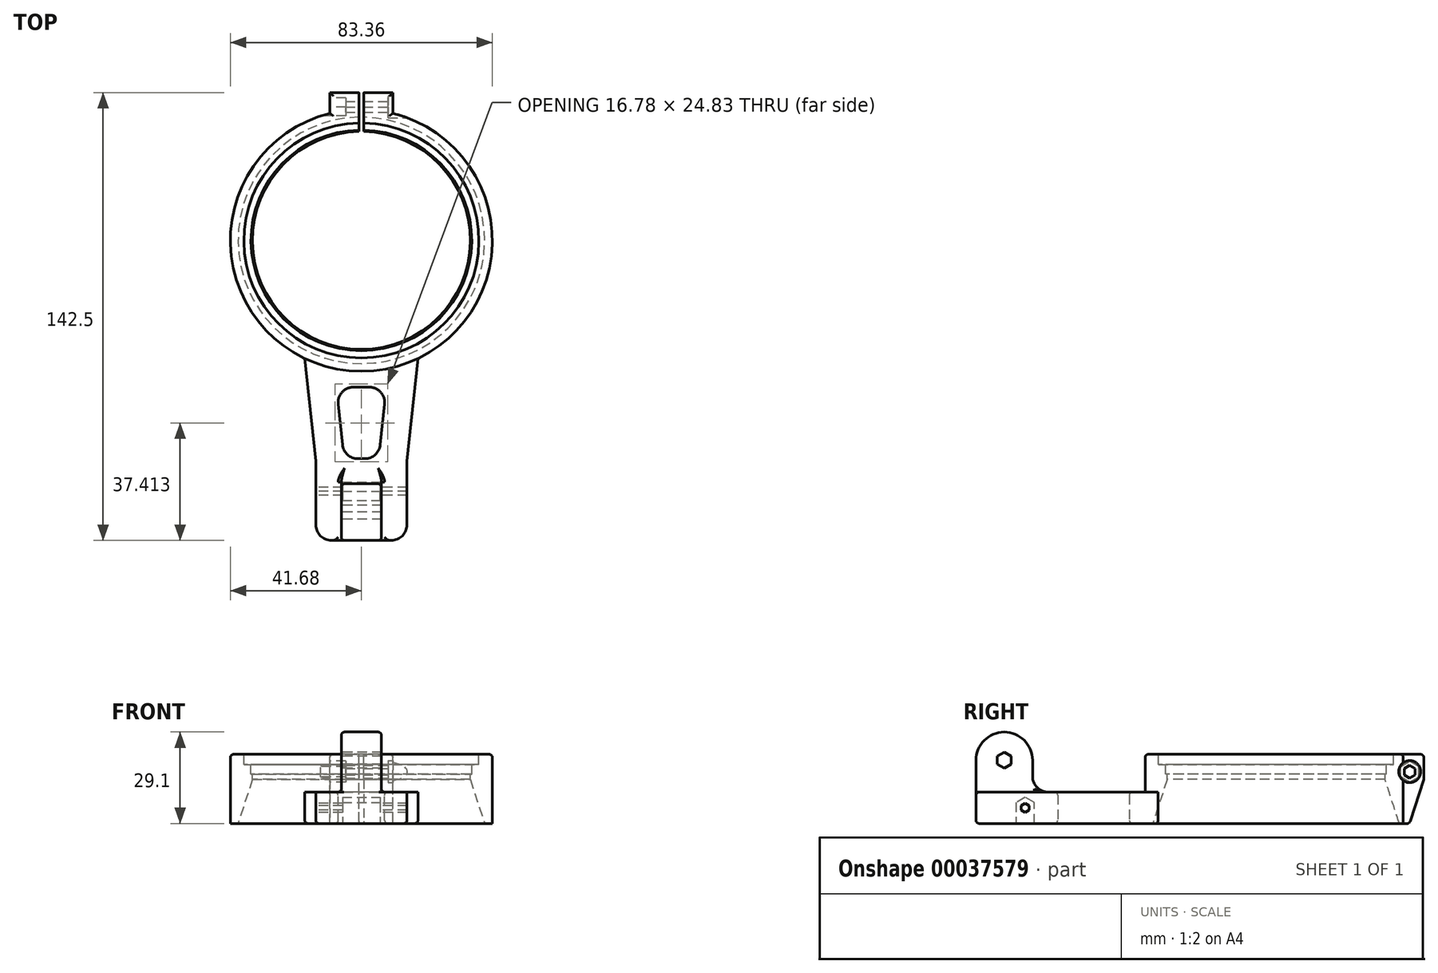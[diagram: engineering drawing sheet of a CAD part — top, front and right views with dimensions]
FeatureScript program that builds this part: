
annotation { "Feature Type Name" : "Feature", "Feature Type Description" : "" }
export const myFeature = defineFeature(function(context is Context, id is Id, definition is map)
    precondition{}
    {
        {
            var Q0;
            Q0=qCreatedBy(makeId("Right.planeOp"),FACE);
            var sketch = newSketch(context, id + "F0", { "sketchPlane" : qUnion([Q0])});
            skLineSegment(sketch, "E0", {"start": v(37.4, 0) * mm, "end": v(41.68, 0) * mm});
            skLineSegment(sketch, "E1", {"start": v(41.68, 0) * mm, "end": v(41.68, 22) * mm});
            skLineSegment(sketch, "E2", {"start": v(41.68, 22) * mm, "end": v(34.68, 22) * mm});
            skLineSegment(sketch, "E3", {"start": v(37.4, 3.3) * mm, "end": v(35.12, 3.3) * mm});
            skLineSegment(sketch, "E4", {"start": v(37.4, 3.3) * mm, "end": v(37.4, 0) * mm});
            skLineSegment(sketch, "E5", {"start": v(0, 0) * mm, "end": v(0, 55.42) * mm, "construction": true});
            skLineSegment(sketch, "E6", {"start": v(35.12, 3.3) * mm, "end": v(35.12, 6.3) * mm});
            skLineSegment(sketch, "E7", {"start": v(35.12, 6.3) * mm, "end": v(34.68, 6.3) * mm});
            skLineSegment(sketch, "E8", {"start": v(34.68, 6.3) * mm, "end": v(34.68, 22) * mm});
            skSolve(sketch);
        }
        {
            var Q0;
            Q0=makeQuery(id+"F0.imprint","IMPRINT",FACE,{"disambiguationData":[TD([[makeQuery(id+"F0.imprint","IMPRINT",EDGE,{"derivedFrom":sQuery(id+"F0.wireOp",EDGE,"E0")}),1.0]])]});
            var Q1;
            Q1=sQuery(id+"F0.wireOp",EDGE,"E5");
            revolve(context, id + "F1", {"entities" : qUnion([Q0]), "axis" : qUnion([Q1]), "revolveType" : RevolveType.FULL});
        }
        {
            var Q0;
            Q0=qCreatedBy(makeId("Top.planeOp"),FACE);
            var sketch = newSketch(context, id + "F2", { "sketchPlane" : qUnion([Q0])});
            skLineSegment(sketch, "E9.bottom", {"start": v(-0.75, 0) * mm, "end": v(0.75, 0) * mm});
            skLineSegment(sketch, "E9.top", {"start": v(-0.75, 47) * mm, "end": v(0.75, 47) * mm});
            skLineSegment(sketch, "E9.left", {"start": v(-0.75, 0) * mm, "end": v(-0.75, 47) * mm});
            skLineSegment(sketch, "E9.right", {"start": v(0.75, 0) * mm, "end": v(0.75, 47) * mm});
            skLineSegment(sketch, "E10", {"start": v(0, 0) * mm, "end": v(0, 47) * mm, "construction": true});
            skLineSegment(sketch, "E11.bottom", {"start": v(-10, 47) * mm, "end": v(10, 47) * mm});
            skLineSegment(sketch, "E11.top", {"start": v(-10, 40.46) * mm, "end": v(10, 40.46) * mm});
            skLineSegment(sketch, "E11.left", {"start": v(-10, 47) * mm, "end": v(-10, 40.46) * mm});
            skLineSegment(sketch, "E11.right", {"start": v(10, 47) * mm, "end": v(10, 40.46) * mm});
            skSolve(sketch);
        }
        {
            var Q0;
            {var subQ1=sQuery(id+"F2.wireOp",EDGE,"E11.left");Q0=makeQuery(id+"F2.imprint","IMPRINT",FACE,{"disambiguationData":[TD([[makeQuery(id+"F2.imprint","IMPRINT",EDGE,{"derivedFrom":subQ1}),1.0]])]});}
            var Q1;
            {var subQ3=sQuery(id+"F2.wireOp",EDGE,"E11.right");Q1=makeQuery(id+"F2.imprint","IMPRINT",FACE,{"disambiguationData":[TD([[makeQuery(id+"F2.imprint","IMPRINT",EDGE,{"derivedFrom":subQ3}),-1.0]])]});}
            var Q2;
            Q2=makeQuery(id+"F1.opRevolve","SWEPT_FACE",FACE,{"disambiguationData":[OSD([sQuery(id+"F0.wireOp",EDGE,"E2")])]});
            extrude(context, id + "F3", {"entities" : qUnion([Q0, Q1]), "operationType" : NewBodyOperationType.ADD, "endBound" : BoundingType.UP_TO_SURFACE, "endBoundEntityFace" : qUnion([Q2]), "depth" : 25 * mm});
        }
        {
            var Q0;
            {var subQ5=sQuery(id+"F2.wireOp",EDGE,"E9.bottom");Q0=makeQuery(id+"F2.imprint","IMPRINT",FACE,{"disambiguationData":[TD([[makeQuery(id+"F2.imprint","IMPRINT",EDGE,{"derivedFrom":subQ5}),1.0]])]});}
            var Q1;
            {var subQ0=sQuery(id+"F2.wireOp",EDGE,"E11.bottom");var subQ3=sQuery(id+"F2.wireOp",EDGE,"E9.left");var subQ4=makeQuery(id+"F2.imprint","INTERSECT",VERTEX,{"derivedFrom":[subQ3,subQ0]});Q1=makeQuery(id+"F2.imprint","IMPRINT",FACE,{"disambiguationData":[TD([[makeQuery(id+"F2.imprint","IMPRINT",EDGE,{"disambiguationData":[TD([[subQ4,1.0]])],"derivedFrom":subQ3}),-1.0]])]});}
            extrude(context, id + "F4", {"entities" : qUnion([Q0, Q1]), "operationType" : NewBodyOperationType.REMOVE, "endBound" : BoundingType.THROUGH_ALL, "depth" : 25 * mm});
        }
        {
            var Q0;
            Q0=makeQuery(id+"F3.opExtrude","SWEPT_FACE",FACE,{"disambiguationData":[OSD([sQuery(id+"F2.wireOp",EDGE,"E11.right")])]});
            var sketch = newSketch(context, id + "F5", { "sketchPlane" : qUnion([Q0])});
            skCircle(sketch, "E12", {"center": v(42.5, 5.5) * mm, "radius": 3.5 * mm});
            skCircle(sketch, "E13.cCircle", {"center": v(42.5, 5.5) * mm, "radius": 1.75 * mm, "construction": true});
            skLineSegment(sketch, "E13.0", {"start": v(44.25, 4.49) * mm, "end": v(42.5, 3.48) * mm});
            skLineSegment(sketch, "E13.1", {"start": v(42.5, 3.48) * mm, "end": v(40.75, 4.49) * mm});
            skLineSegment(sketch, "E13.2", {"start": v(40.75, 4.49) * mm, "end": v(40.75, 6.51) * mm});
            skLineSegment(sketch, "E13.3", {"start": v(40.75, 6.51) * mm, "end": v(42.5, 7.52) * mm});
            skLineSegment(sketch, "E13.4", {"start": v(42.5, 7.52) * mm, "end": v(44.25, 6.51) * mm});
            skLineSegment(sketch, "E13.5", {"start": v(44.25, 6.51) * mm, "end": v(44.25, 4.49) * mm});
            skPoint(sketch, "E13.0.midPoint", {"position": v(43.38, 3.98) * mm});
            skSolve(sketch);
        }
        {
            var Q0;
            {var subQ5=sQuery(id+"F5.wireOp",EDGE,"E13.2");Q0=makeQuery(id+"F5.imprint","IMPRINT",FACE,{"disambiguationData":[TD([[makeQuery(id+"F5.imprint","IMPRINT",EDGE,{"derivedFrom":subQ5}),-1.0]])]});}
            var Q1;
            {var subQ5=sQuery(id+"F5.wireOp",EDGE,"E13.0");Q1=makeQuery(id+"F5.imprint","IMPRINT",FACE,{"disambiguationData":[TD([[makeQuery(id+"F5.imprint","IMPRINT",EDGE,{"derivedFrom":subQ5}),-1.0]])]});}
            extrude(context, id + "F6", {"entities" : qUnion([Q0, Q1]), "operationType" : NewBodyOperationType.REMOVE, "endBound" : BoundingType.THROUGH_ALL, "oppositeDirection" : true, "depth" : 25 * mm, "hasSecondDirection" : true, "secondDirectionBound" : SecondDirectionBoundingType.THROUGH_ALL, "secondDirectionOppositeDirection" : false, "secondDirectionDepth" : 25 * mm});
        }
        {
            var Q0;
            {var subQ8=sQuery(id+"F5.wireOp",EDGE,"E13.2");Q0=makeQuery(id+"F5.imprint","IMPRINT",FACE,{"disambiguationData":[TD([[makeQuery(id+"F5.imprint","IMPRINT",EDGE,{"derivedFrom":subQ8}),1.0]])]});}
            var Q1;
            {var subQ7=sQuery(id+"F5.wireOp",EDGE,"E13.0");Q1=makeQuery(id+"F5.imprint","IMPRINT",FACE,{"disambiguationData":[TD([[makeQuery(id+"F5.imprint","IMPRINT",EDGE,{"derivedFrom":subQ7}),1.0]])]});}
            var Q2;
            {var subQ0=sQuery(id+"F5.wireOp",EDGE,"E12");var subQ1=makeQuery(id+"F3.opExtrude","SWEPT_EDGE",EDGE,{"disambiguationData":[OSD([sQuery(id+"F2.wireOp",EDGE,"E11.top"),sQuery(id+"F2.wireOp",EDGE,"E11.right")])]});var subQ2=makeQuery(id+"F5.imprint","INTERSECT",VERTEX,{"disambiguationData":[OD(0.0)],"derivedFrom":[subQ1,subQ0]});Q2=makeQuery(id+"F5.imprint","IMPRINT",FACE,{"disambiguationData":[TD([[makeQuery(id+"F5.imprint","IMPRINT",EDGE,{"disambiguationData":[TD([[subQ2,1.0]])],"derivedFrom":subQ0}),1.0]])]});}
            extrude(context, id + "F7", {"entities" : qUnion([Q0, Q1, Q2]), "operationType" : NewBodyOperationType.REMOVE, "oppositeDirection" : true, "depth" : 1.5 * mm, "hasSecondDirection" : true, "secondDirectionBound" : SecondDirectionBoundingType.THROUGH_ALL, "secondDirectionOppositeDirection" : false, "secondDirectionDepth" : 25 * mm});
        }
        {
            var Q0;
            Q0=makeQuery(id+"F3.opExtrude","SWEPT_FACE",FACE,{"disambiguationData":[OSD([sQuery(id+"F2.wireOp",EDGE,"E11.left")])]});
            var sketch = newSketch(context, id + "F8", { "sketchPlane" : qUnion([Q0])});
            skCircle(sketch, "E14.cCircle", {"center": v(-42.5, 5.5) * mm, "radius": 2.9 * mm, "construction": true});
            skLineSegment(sketch, "E14.0", {"start": v(-42.5, 2.15) * mm, "end": v(-45.4, 3.83) * mm});
            skLineSegment(sketch, "E14.1", {"start": v(-45.4, 3.83) * mm, "end": v(-45.4, 7.17) * mm});
            skLineSegment(sketch, "E14.2", {"start": v(-45.4, 7.17) * mm, "end": v(-42.5, 8.85) * mm});
            skLineSegment(sketch, "E14.3", {"start": v(-42.5, 8.85) * mm, "end": v(-39.6, 7.17) * mm});
            skLineSegment(sketch, "E14.4", {"start": v(-39.6, 7.17) * mm, "end": v(-39.6, 3.83) * mm});
            skLineSegment(sketch, "E14.5", {"start": v(-39.6, 3.83) * mm, "end": v(-42.5, 2.15) * mm});
            skPoint(sketch, "E14.0.midPoint", {"position": v(-43.95, 2.99) * mm});
            skSolve(sketch);
        }
        {
            var Q0;
            {var subQ5=sQuery(id+"F8.wireOp",EDGE,"E14.4");Q0=makeQuery(id+"F8.imprint","IMPRINT",FACE,{"disambiguationData":[TD([[makeQuery(id+"F8.imprint","IMPRINT",EDGE,{"derivedFrom":subQ5}),-1.0]])]});}
            var Q1;
            {var subQ6=sQuery(id+"F8.wireOp",EDGE,"E14.0");Q1=makeQuery(id+"F8.imprint","IMPRINT",FACE,{"disambiguationData":[TD([[makeQuery(id+"F8.imprint","IMPRINT",EDGE,{"derivedFrom":subQ6}),-1.0]])]});}
            var Q2;
            Q2=sQuery(id+"F8.wireOp",EDGE,"E14.5");
            var Q3;
            Q3=sQuery(id+"F8.wireOp",EDGE,"E14.4");
            var Q4;
            Q4=sQuery(id+"F8.wireOp",EDGE,"E14.3");
            var Q5;
            Q5=sQuery(id+"F8.wireOp",EDGE,"E14.2");
            var Q6;
            Q6=sQuery(id+"F8.wireOp",EDGE,"E14.1");
            var Q7;
            Q7=sQuery(id+"F8.wireOp",EDGE,"E14.0");
            extrude(context, id + "F9", {"entities" : qUnion([Q0, Q1]), "operationType" : NewBodyOperationType.REMOVE, "surfaceEntities" : qUnion([Q2, Q3, Q4, Q5, Q6, Q7]), "oppositeDirection" : true, "depth" : 5 * mm, "hasSecondDirection" : true, "secondDirectionBound" : SecondDirectionBoundingType.THROUGH_ALL, "secondDirectionOppositeDirection" : false, "secondDirectionDepth" : 25 * mm});
        }
        {
            var Q0;
            {var subQ0=sQuery(id+"F2.wireOp",EDGE,"E11.top");var subQ1=sQuery(id+"F2.wireOp",EDGE,"E11.bottom");Q0=makeQuery(id+"F3.boolean.opBoolean","MERGE",FACE,{"derivedFrom":[makeQuery(id+"F1.opRevolve","SWEPT_FACE",FACE,{"disambiguationData":[OSD([sQuery(id+"F0.wireOp",EDGE,"E2")])]}),makeQuery(id+"F3.opExtrude","CAP_FACE",FACE,{"disambiguationData":[OSD([sQuery(id+"F2.wireOp",EDGE,"E9.left"),subQ1,subQ0,sQuery(id+"F2.wireOp",EDGE,"E11.left")])],"isStart":false}),makeQuery(id+"F3.opExtrude","CAP_FACE",FACE,{"disambiguationData":[OSD([sQuery(id+"F2.wireOp",EDGE,"E9.right"),subQ1,subQ0,sQuery(id+"F2.wireOp",EDGE,"E11.right")])],"isStart":false})]});}
            var sketch = newSketch(context, id + "F10", { "sketchPlane" : qUnion([Q0])});
            skLineSegment(sketch, "E15", {"start": v(0, 0) * mm, "end": v(0, -95.5) * mm, "construction": true});
            skLineSegment(sketch, "E16.bottom", {"start": v(18, -37.59) * mm, "end": v(-18, -37.59) * mm});
            skLineSegment(sketch, "E16.top", {"start": v(14.5, -95.5) * mm, "end": v(-14.5, -95.5) * mm});
            skLineSegment(sketch, "E16.left", {"start": v(18, -37.59) * mm, "end": v(14.5, -70.5) * mm});
            skLineSegment(sketch, "E16.right", {"start": v(-18, -37.59) * mm, "end": v(-14.5, -70.5) * mm});
            skLineSegment(sketch, "E17", {"start": v(6.38, -77.5) * mm, "end": v(-6.37, -77.5) * mm});
            skLineSegment(sketch, "E18", {"start": v(6.38, -95.5) * mm, "end": v(6.38, -77.5) * mm});
            skLineSegment(sketch, "E19", {"start": v(-6.37, -95.5) * mm, "end": v(-6.37, -77.5) * mm});
            skLineSegment(sketch, "E20", {"start": v(14.5, -95.5) * mm, "end": v(14.5, -70.5) * mm});
            skLineSegment(sketch, "E21", {"start": v(-14.5, -95.5) * mm, "end": v(-14.5, -70.5) * mm});
            skLineSegment(sketch, "E22", {"start": v(-7.98, -46.68) * mm, "end": v(-5.56, -69.5) * mm});
            skLineSegment(sketch, "E23", {"start": v(-5.56, -69.5) * mm, "end": v(5.56, -69.5) * mm});
            skLineSegment(sketch, "E24", {"start": v(5.56, -69.5) * mm, "end": v(7.98, -46.68) * mm});
            skLineSegment(sketch, "E25", {"start": v(7.98, -46.68) * mm, "end": v(-7.98, -46.68) * mm});
            skSolve(sketch);
        }
        {
            var Q0;
            {var subQ12=sQuery(id+"F10.wireOp",EDGE,"E17");Q0=makeQuery(id+"F10.imprint","IMPRINT",FACE,{"disambiguationData":[TD([[makeQuery(id+"F10.imprint","IMPRINT",EDGE,{"derivedFrom":subQ12}),-1.0]])]});}
            var Q1;
            Q1=makeQuery(id+"F10.imprint","IMPRINT",FACE,{"disambiguationData":[TD([[makeQuery(id+"F10.imprint","IMPRINT",EDGE,{"derivedFrom":sQuery(id+"F10.wireOp",EDGE,"E17")}),1.0]])]});
            extrude(context, id + "F11", {"entities" : qUnion([Q0, Q1]), "operationType" : NewBodyOperationType.ADD, "oppositeDirection" : true, "depth" : 10 * mm});
        }
        {
            var Q0;
            Q0=makeQuery(id+"F10.imprint","IMPRINT",FACE,{"disambiguationData":[TD([[makeQuery(id+"F10.imprint","IMPRINT",EDGE,{"derivedFrom":sQuery(id+"F10.wireOp",EDGE,"E17")}),1.0]])]});
            extrude(context, id + "F12", {"entities" : qUnion([Q0]), "operationType" : NewBodyOperationType.ADD, "oppositeDirection" : true, "depth" : 29.1 * mm});
        }
        {
            var Q0;
            Q0=makeQuery(id+"F11.opExtrude","SWEPT_FACE",FACE,{"disambiguationData":[OSD([sQuery(id+"F10.wireOp",EDGE,"E20")])]});
            var sketch = newSketch(context, id + "F13", { "sketchPlane" : qUnion([Q0])});
            skCircle(sketch, "E26.cCircle", {"center": v(-86.5, 1.9) * mm, "radius": 2.2 * mm, "construction": true});
            skLineSegment(sketch, "E26.0", {"start": v(-88.7, 3.17) * mm, "end": v(-86.5, 4.44) * mm});
            skLineSegment(sketch, "E26.1", {"start": v(-86.5, 4.44) * mm, "end": v(-84.3, 3.17) * mm});
            skLineSegment(sketch, "E26.2", {"start": v(-84.3, 3.17) * mm, "end": v(-84.3, 0.63) * mm});
            skLineSegment(sketch, "E26.3", {"start": v(-84.3, 0.63) * mm, "end": v(-86.5, -0.64) * mm});
            skLineSegment(sketch, "E26.4", {"start": v(-86.5, -0.64) * mm, "end": v(-88.7, 0.63) * mm});
            skLineSegment(sketch, "E26.5", {"start": v(-88.7, 0.63) * mm, "end": v(-88.7, 3.17) * mm});
            skPoint(sketch, "E26.0.midPoint", {"position": v(-87.6, 3.8) * mm});
            skCircle(sketch, "E27.cCircle", {"center": v(-79.85, 17) * mm, "radius": 1.25 * mm, "construction": true});
            skLineSegment(sketch, "E27.0", {"start": v(-81.1, 17.72) * mm, "end": v(-79.85, 18.44) * mm});
            skLineSegment(sketch, "E27.1", {"start": v(-79.85, 18.44) * mm, "end": v(-78.6, 17.72) * mm});
            skLineSegment(sketch, "E27.2", {"start": v(-78.6, 17.72) * mm, "end": v(-78.6, 16.28) * mm});
            skLineSegment(sketch, "E27.3", {"start": v(-78.6, 16.28) * mm, "end": v(-79.85, 15.56) * mm});
            skLineSegment(sketch, "E27.4", {"start": v(-79.85, 15.56) * mm, "end": v(-81.1, 16.28) * mm});
            skLineSegment(sketch, "E27.5", {"start": v(-81.1, 16.28) * mm, "end": v(-81.1, 17.72) * mm});
            skPoint(sketch, "E27.0.midPoint", {"position": v(-80.47, 18.08) * mm});
            skCircle(sketch, "E28.cCircle", {"center": v(-79.85, 17) * mm, "radius": 2.9 * mm, "construction": true});
            skLineSegment(sketch, "E28.2", {"start": v(-76.95, 18.67) * mm, "end": v(-76.95, 15.33) * mm});
            skLineSegment(sketch, "E28.3", {"start": v(-76.95, 15.33) * mm, "end": v(-79.85, 13.65) * mm});
            skLineSegment(sketch, "E28.4", {"start": v(-79.85, 13.65) * mm, "end": v(-82.75, 15.33) * mm});
            skLineSegment(sketch, "E28.5", {"start": v(-82.75, 15.33) * mm, "end": v(-82.75, 22) * mm});
            skLineSegment(sketch, "E29", {"start": v(-82.75, 22) * mm, "end": v(-76.95, 22) * mm});
            skLineSegment(sketch, "E30", {"start": v(-76.95, 22) * mm, "end": v(-76.95, 18.67) * mm});
            skSolve(sketch);
        }
        {
            var Q0;
            Q0=makeQuery(id+"F13.imprint","IMPRINT",FACE,{"disambiguationData":[TD([[makeQuery(id+"F13.imprint","IMPRINT",EDGE,{"derivedFrom":sQuery(id+"F13.wireOp",EDGE,"E26.0")}),-1.0]])]});
            var Q1;
            Q1=makeQuery(id+"F13.imprint","IMPRINT",FACE,{"disambiguationData":[TD([[makeQuery(id+"F13.imprint","IMPRINT",EDGE,{"derivedFrom":sQuery(id+"F13.wireOp",EDGE,"E27.0")}),-1.0]])]});
            extrude(context, id + "F14", {"entities" : qUnion([Q0, Q1]), "operationType" : NewBodyOperationType.REMOVE, "endBound" : BoundingType.THROUGH_ALL, "depth" : 25 * mm, "hasSecondDirection" : true, "secondDirectionBound" : SecondDirectionBoundingType.THROUGH_ALL, "secondDirectionOppositeDirection" : true, "secondDirectionDepth" : 25 * mm});
        }
        {
            var Q0;
            Q0=makeQuery(id+"F13.imprint","IMPRINT",FACE,{"disambiguationData":[TD([[makeQuery(id+"F13.imprint","IMPRINT",EDGE,{"derivedFrom":sQuery(id+"F13.wireOp",EDGE,"E27.0")}),1.0]])]});
            extrude(context, id + "F15", {"entities" : qUnion([Q0]), "operationType" : NewBodyOperationType.REMOVE, "oppositeDirection" : true, "depth" : 20.5 * mm, "hasSecondDirection" : true, "secondDirectionOppositeDirection" : true, "secondDirectionDepth" : 8.5 * mm});
        }
        {
            var Q0;
            Q0=makeQuery(id+"F12.opExtrude","CAP_EDGE",EDGE,{"disambiguationData":[OSD([sQuery(id+"F10.wireOp",EDGE,"E16.top")])],"isStart":false});
            var Q1;
            Q1=makeQuery(id+"F12.opExtrude","CAP_EDGE",EDGE,{"disambiguationData":[OSD([sQuery(id+"F10.wireOp",EDGE,"E17")])],"isStart":false});
            fillet(context, id + "F16", {"entities" : qUnion([Q0, Q1]), "radius" : 9 * mm, "tangentPropagation" : true, "allowEdgeOverflow" : false});
        }
        {
            var Q0;
            Q0=makeQuery(id+"F1.opRevolve","SWEPT_EDGE",EDGE,{"disambiguationData":[OSD([sQuery(id+"F0.wireOp",EDGE,"E2"),sQuery(id+"F0.wireOp",EDGE,"E8")])]});
            var Q1;
            {var subQ0=sQuery(id+"F2.wireOp",EDGE,"E11.bottom");Q1=makeQuery(id+"F3.opExtrude","CAP_EDGE",EDGE,{"disambiguationData":[OSD([subQ0]),TDD([makeQuery(id+"F2.imprint","IMPRINT",EDGE,{"disambiguationData":[TD([[makeQuery(id+"F2.imprint","INTERSECT",VERTEX,{"derivedFrom":[sQuery(id+"F2.wireOp",EDGE,"E9.left"),subQ0]}),1.0]])],"derivedFrom":subQ0})])],"isStart":false});}
            var Q2;
            {var subQ0=sQuery(id+"F2.wireOp",EDGE,"E11.bottom");Q2=makeQuery(id+"F3.opExtrude","CAP_EDGE",EDGE,{"disambiguationData":[OSD([subQ0]),TDD([makeQuery(id+"F2.imprint","IMPRINT",EDGE,{"disambiguationData":[TD([[makeQuery(id+"F2.imprint","INTERSECT",VERTEX,{"derivedFrom":[sQuery(id+"F2.wireOp",EDGE,"E9.right"),subQ0]}),-1.0]])],"derivedFrom":subQ0})])],"isStart":false});}
            chamfer(context, id + "F17", {"entities" : qUnion([Q0, Q1, Q2]), "chamferType" : ChamferType.OFFSET_ANGLE, "width" : 14 * mm, "oppositeDirection" : true, "angle" : 18 * degree, "tangentPropagation" : true});
        }
        {
            var Q0;
            {var subQ0=sQuery(id+"F2.wireOp",EDGE,"E11.bottom");Q0=makeQuery(id+"F3.opExtrude","CAP_EDGE",EDGE,{"disambiguationData":[OSD([subQ0]),TDD([makeQuery(id+"F2.imprint","IMPRINT",EDGE,{"disambiguationData":[TD([[makeQuery(id+"F2.imprint","INTERSECT",VERTEX,{"derivedFrom":[sQuery(id+"F2.wireOp",EDGE,"E9.right"),subQ0]}),-1.0]])],"derivedFrom":subQ0})])],"isStart":true});}
            var Q1;
            {var subQ0=sQuery(id+"F2.wireOp",EDGE,"E11.bottom");Q1=makeQuery(id+"F3.opExtrude","CAP_EDGE",EDGE,{"disambiguationData":[OSD([subQ0]),TDD([makeQuery(id+"F2.imprint","IMPRINT",EDGE,{"disambiguationData":[TD([[makeQuery(id+"F2.imprint","INTERSECT",VERTEX,{"derivedFrom":[sQuery(id+"F2.wireOp",EDGE,"E9.left"),subQ0]}),1.0]])],"derivedFrom":subQ0})])],"isStart":true});}
            var Q2;
            {var subQ3=sQuery(id+"F2.wireOp",EDGE,"E11.left");var subQ4=sQuery(id+"F0.wireOp",EDGE,"E1");var subQ5=sQuery(id+"F0.wireOp",EDGE,"E0");Q2=makeQuery(id+"F3.boolean.opBoolean","SPLIT",EDGE,{"disambiguationData":[TD([makeQuery(id+"F3.opExtrude","SWEPT_FACE",FACE,{"disambiguationData":[OSD([subQ3])]})])],"derivedFrom":makeQuery(id+"F1.opRevolve","SWEPT_EDGE",EDGE,{"disambiguationData":[OSD([subQ5,subQ4])]})});}
            var Q3;
            Q3=makeQuery(id+"F3.opExtrude","CAP_EDGE",EDGE,{"disambiguationData":[OSD([sQuery(id+"F2.wireOp",EDGE,"E11.right")])],"isStart":true});
            var Q4;
            Q4=makeQuery(id+"F3.opExtrude","CAP_EDGE",EDGE,{"disambiguationData":[OSD([sQuery(id+"F2.wireOp",EDGE,"E11.left")])],"isStart":true});
            fillet(context, id + "F18", {"entities" : qUnion([Q0, Q1, Q2, Q3, Q4]), "radius" : 1 * mm, "tangentPropagation" : true, "allowEdgeOverflow" : false});
        }
        {
            var Q0;
            Q0=makeQuery(id+"F1.opRevolve","SWEPT_BODY",BODY,{"disambiguationData":[OSD([sQuery(id+"F0.wireOp",EDGE,"E0"),sQuery(id+"F0.wireOp",EDGE,"E1"),sQuery(id+"F0.wireOp",EDGE,"E2"),sQuery(id+"F0.wireOp",EDGE,"E3"),sQuery(id+"F0.wireOp",EDGE,"E4"),sQuery(id+"F0.wireOp",EDGE,"E6"),sQuery(id+"F0.wireOp",EDGE,"E7"),sQuery(id+"F0.wireOp",EDGE,"E8")])]});
            var Q1;
            {var subQ0=sQuery(id+"F2.wireOp",EDGE,"E11.top");var subQ1=sQuery(id+"F2.wireOp",EDGE,"E11.bottom");Q1=makeQuery(id+"F3.boolean.opBoolean","MERGE",FACE,{"derivedFrom":[makeQuery(id+"F1.opRevolve","SWEPT_FACE",FACE,{"disambiguationData":[OSD([sQuery(id+"F0.wireOp",EDGE,"E0")])]}),makeQuery(id+"F3.opExtrude","CAP_FACE",FACE,{"disambiguationData":[OSD([sQuery(id+"F2.wireOp",EDGE,"E9.left"),subQ1,subQ0,sQuery(id+"F2.wireOp",EDGE,"E11.left")])],"isStart":true}),makeQuery(id+"F3.opExtrude","CAP_FACE",FACE,{"disambiguationData":[OSD([sQuery(id+"F2.wireOp",EDGE,"E9.right"),subQ1,subQ0,sQuery(id+"F2.wireOp",EDGE,"E11.right")])],"isStart":true})]});}
            var Q2;
            Q2=qCreatedBy(makeId("Top.planeOp"),FACE);
            mirror(context, id + "F19", {"entities" : qUnion([Q0]), "faces" : qUnion([Q1]), "mirrorPlane" : qUnion([Q2])});
        }
        {
            var Q0;
            Q0=makeQuery(id+"F1.opRevolve","SWEPT_BODY",BODY,{"disambiguationData":[OSD([sQuery(id+"F0.wireOp",EDGE,"E0"),sQuery(id+"F0.wireOp",EDGE,"E1"),sQuery(id+"F0.wireOp",EDGE,"E2"),sQuery(id+"F0.wireOp",EDGE,"E3"),sQuery(id+"F0.wireOp",EDGE,"E4"),sQuery(id+"F0.wireOp",EDGE,"E6"),sQuery(id+"F0.wireOp",EDGE,"E7"),sQuery(id+"F0.wireOp",EDGE,"E8")])]});
            deleteBodies(context, id + "F20", {"entities" : qUnion([Q0])});
        }
        {
            var Q0;
            Q0=makeQuery(id+"F19.opPattern","COPY",BODY,{"derivedFrom":makeQuery(id+"F1.opRevolve","SWEPT_BODY",BODY,{"disambiguationData":[OSD([sQuery(id+"F0.wireOp",EDGE,"E0"),sQuery(id+"F0.wireOp",EDGE,"E1"),sQuery(id+"F0.wireOp",EDGE,"E2"),sQuery(id+"F0.wireOp",EDGE,"E3"),sQuery(id+"F0.wireOp",EDGE,"E4"),sQuery(id+"F0.wireOp",EDGE,"E6"),sQuery(id+"F0.wireOp",EDGE,"E7"),sQuery(id+"F0.wireOp",EDGE,"E8")])]}),"instanceName":"1"});
            var Q1;
            Q1=qCreatedBy(makeId("Top.planeOp"),FACE);
            transform(context, id + "F21", {"entities" : qUnion([Q0]), "transformType" : TransformType.TRANSLATION_DISTANCE, "transformDirection" : qUnion([Q1]), "distance" : 22 * mm, "makeCopy" : false});
        }
        {
            var Q0;
            Q0=makeQuery(id+"F19.opPattern","COPY",EDGE,{"derivedFrom":makeQuery(id+"F11.opExtrude","CAP_EDGE",EDGE,{"disambiguationData":[OSD([sQuery(id+"F0.wireOp",EDGE,"E1"),sQuery(id+"F0.wireOp",EDGE,"E2")])],"isStart":false}),"instanceName":"1"});
            var Q1;
            Q1=makeQuery(id+"F19.opPattern","COPY",EDGE,{"derivedFrom":makeQuery(id+"F11.opExtrude","SWEPT_EDGE",EDGE,{"disambiguationData":[OSD([sQuery(id+"F0.wireOp",EDGE,"E1"),sQuery(id+"F0.wireOp",EDGE,"E2"),sQuery(id+"F10.wireOp",EDGE,"E16.bottom"),sQuery(id+"F10.wireOp",EDGE,"E16.left")])]}),"instanceName":"1"});
            var Q2;
            Q2=makeQuery(id+"F19.opPattern","COPY",EDGE,{"derivedFrom":makeQuery(id+"F11.opExtrude","SWEPT_EDGE",EDGE,{"disambiguationData":[OSD([sQuery(id+"F0.wireOp",EDGE,"E1"),sQuery(id+"F0.wireOp",EDGE,"E2"),sQuery(id+"F10.wireOp",EDGE,"E16.bottom"),sQuery(id+"F10.wireOp",EDGE,"E16.right")])]}),"instanceName":"1"});
            var Q3;
            Q3=makeQuery(id+"F19.opPattern","COPY",EDGE,{"derivedFrom":makeQuery(id+"F11.opExtrude","SWEPT_EDGE",EDGE,{"disambiguationData":[OSD([sQuery(id+"F10.wireOp",EDGE,"E16.top"),sQuery(id+"F10.wireOp",EDGE,"E20")])]}),"instanceName":"1"});
            var Q4;
            Q4=makeQuery(id+"F19.opPattern","COPY",EDGE,{"derivedFrom":makeQuery(id+"F11.opExtrude","SWEPT_EDGE",EDGE,{"disambiguationData":[OSD([sQuery(id+"F10.wireOp",EDGE,"E16.top"),sQuery(id+"F10.wireOp",EDGE,"E21")])]}),"instanceName":"1"});
            var Q5;
            Q5=makeQuery(id+"F19.opPattern","COPY",EDGE,{"derivedFrom":makeQuery(id+"F11.opExtrude","SWEPT_EDGE",EDGE,{"disambiguationData":[OSD([sQuery(id+"F10.wireOp",EDGE,"E16.right"),sQuery(id+"F10.wireOp",EDGE,"E21")])]}),"instanceName":"1"});
            var Q6;
            Q6=makeQuery(id+"F19.opPattern","COPY",EDGE,{"derivedFrom":makeQuery(id+"F11.opExtrude","SWEPT_EDGE",EDGE,{"disambiguationData":[OSD([sQuery(id+"F10.wireOp",EDGE,"E16.left"),sQuery(id+"F10.wireOp",EDGE,"E20")])]}),"instanceName":"1"});
            var Q7;
            Q7=makeQuery(id+"F19.opPattern","COPY",EDGE,{"derivedFrom":makeQuery(id+"F11.opExtrude","SWEPT_EDGE",EDGE,{"disambiguationData":[OSD([sQuery(id+"F10.wireOp",EDGE,"E24"),sQuery(id+"F10.wireOp",EDGE,"E25")])]}),"instanceName":"1"});
            var Q8;
            Q8=makeQuery(id+"F19.opPattern","COPY",EDGE,{"derivedFrom":makeQuery(id+"F11.opExtrude","SWEPT_EDGE",EDGE,{"disambiguationData":[OSD([sQuery(id+"F10.wireOp",EDGE,"E22"),sQuery(id+"F10.wireOp",EDGE,"E25")])]}),"instanceName":"1"});
            var Q9;
            Q9=makeQuery(id+"F19.opPattern","COPY",EDGE,{"derivedFrom":makeQuery(id+"F11.opExtrude","SWEPT_EDGE",EDGE,{"disambiguationData":[OSD([sQuery(id+"F10.wireOp",EDGE,"E23"),sQuery(id+"F10.wireOp",EDGE,"E24")])]}),"instanceName":"1"});
            var Q10;
            Q10=makeQuery(id+"F19.opPattern","COPY",EDGE,{"derivedFrom":makeQuery(id+"F11.opExtrude","SWEPT_EDGE",EDGE,{"disambiguationData":[OSD([sQuery(id+"F10.wireOp",EDGE,"E22"),sQuery(id+"F10.wireOp",EDGE,"E23")])]}),"instanceName":"1"});
            var Q11;
            Q11=makeQuery(id+"F19.opPattern","COPY",EDGE,{"derivedFrom":makeQuery(id+"F12.boolean.opBoolean","INTERSECT",EDGE,{"derivedFrom":[makeQuery(id+"F11.opExtrude","CAP_FACE",FACE,{"disambiguationData":[OSD([sQuery(id+"F0.wireOp",EDGE,"E1"),sQuery(id+"F0.wireOp",EDGE,"E2"),sQuery(id+"F10.wireOp",EDGE,"E16.top"),sQuery(id+"F10.wireOp",EDGE,"E16.left"),sQuery(id+"F10.wireOp",EDGE,"E16.right"),sQuery(id+"F10.wireOp",EDGE,"E20"),sQuery(id+"F10.wireOp",EDGE,"E21"),sQuery(id+"F10.wireOp",EDGE,"E22"),sQuery(id+"F10.wireOp",EDGE,"E23"),sQuery(id+"F10.wireOp",EDGE,"E24"),sQuery(id+"F10.wireOp",EDGE,"E25")])],"isStart":false}),makeQuery(id+"F12.opExtrude","SWEPT_FACE",FACE,{"disambiguationData":[OSD([sQuery(id+"F10.wireOp",EDGE,"E17")])]})]}),"instanceName":"1"});
            fillet(context, id + "F22", {"entities" : qUnion([Q0, Q1, Q2, Q3, Q4, Q5, Q6, Q7, Q8, Q9, Q10, Q11]), "radius" : 5 * mm, "tangentPropagation" : true, "allowEdgeOverflow" : false});
        }
        {
            var Q0;
            Q0=makeQuery(id+"F19.opPattern","COPY",EDGE,{"derivedFrom":makeQuery(id+"F11.opExtrude","CAP_EDGE",EDGE,{"disambiguationData":[OSD([sQuery(id+"F10.wireOp",EDGE,"E16.right")])],"isStart":true}),"instanceName":"1"});
            var Q1;
            Q1=makeQuery(id+"F19.opPattern","COPY",EDGE,{"derivedFrom":makeQuery(id+"F12.boolean.opBoolean","INTERSECT",EDGE,{"derivedFrom":[makeQuery(id+"F11.opExtrude","CAP_FACE",FACE,{"disambiguationData":[OSD([sQuery(id+"F0.wireOp",EDGE,"E1"),sQuery(id+"F0.wireOp",EDGE,"E2"),sQuery(id+"F10.wireOp",EDGE,"E16.top"),sQuery(id+"F10.wireOp",EDGE,"E16.left"),sQuery(id+"F10.wireOp",EDGE,"E16.right"),sQuery(id+"F10.wireOp",EDGE,"E20"),sQuery(id+"F10.wireOp",EDGE,"E21"),sQuery(id+"F10.wireOp",EDGE,"E22"),sQuery(id+"F10.wireOp",EDGE,"E23"),sQuery(id+"F10.wireOp",EDGE,"E24"),sQuery(id+"F10.wireOp",EDGE,"E25")])],"isStart":false}),makeQuery(id+"F12.opExtrude","SWEPT_FACE",FACE,{"disambiguationData":[OSD([sQuery(id+"F10.wireOp",EDGE,"E19")])]})]}),"instanceName":"1"});
            var Q2;
            Q2=makeQuery(id+"F19.opPattern","COPY",EDGE,{"derivedFrom":makeQuery(id+"F12.boolean.opBoolean","INTERSECT",EDGE,{"derivedFrom":[makeQuery(id+"F11.opExtrude","CAP_FACE",FACE,{"disambiguationData":[OSD([sQuery(id+"F0.wireOp",EDGE,"E1"),sQuery(id+"F0.wireOp",EDGE,"E2"),sQuery(id+"F10.wireOp",EDGE,"E16.top"),sQuery(id+"F10.wireOp",EDGE,"E16.left"),sQuery(id+"F10.wireOp",EDGE,"E16.right"),sQuery(id+"F10.wireOp",EDGE,"E20"),sQuery(id+"F10.wireOp",EDGE,"E21"),sQuery(id+"F10.wireOp",EDGE,"E22"),sQuery(id+"F10.wireOp",EDGE,"E23"),sQuery(id+"F10.wireOp",EDGE,"E24"),sQuery(id+"F10.wireOp",EDGE,"E25")])],"isStart":false}),makeQuery(id+"F12.opExtrude","SWEPT_FACE",FACE,{"disambiguationData":[OSD([sQuery(id+"F10.wireOp",EDGE,"E18")])]})]}),"instanceName":"1"});
            var Q3;
            {var subQ0=sQuery(id+"F0.wireOp",EDGE,"E2");var subQ1=sQuery(id+"F2.wireOp",EDGE,"E11.top");var subQ2=sQuery(id+"F2.wireOp",EDGE,"E11.bottom");var subQ3=sQuery(id+"F2.wireOp",EDGE,"E11.left");var subQ4=sQuery(id+"F2.wireOp",EDGE,"E9.left");Q3=makeQuery(id+"F19.opPattern","COPY",EDGE,{"derivedFrom":makeQuery(id+"F17.opChamfer","BLEND_EDGE",EDGE,{"blendedFrom":[makeQuery(id+"F3.opExtrude","CAP_EDGE",EDGE,{"disambiguationData":[OSD([subQ2]),TDD([makeQuery(id+"F2.imprint","IMPRINT",EDGE,{"disambiguationData":[TD([[makeQuery(id+"F2.imprint","INTERSECT",VERTEX,{"derivedFrom":[subQ4,subQ2]}),1.0]])],"derivedFrom":subQ2})])],"isStart":false}),makeQuery(id+"F11.boolean.opBoolean","MERGE",FACE,{"derivedFrom":[makeQuery(id+"F3.boolean.opBoolean","MERGE",FACE,{"derivedFrom":[makeQuery(id+"F1.opRevolve","SWEPT_FACE",FACE,{"disambiguationData":[OSD([subQ0])]}),makeQuery(id+"F3.opExtrude","CAP_FACE",FACE,{"disambiguationData":[OSD([subQ4,subQ2,subQ1,subQ3])],"isStart":false}),makeQuery(id+"F3.opExtrude","CAP_FACE",FACE,{"disambiguationData":[OSD([sQuery(id+"F2.wireOp",EDGE,"E9.right"),subQ2,subQ1,sQuery(id+"F2.wireOp",EDGE,"E11.right")])],"isStart":false})]}),makeQuery(id+"F11.opExtrude","CAP_FACE",FACE,{"disambiguationData":[OSD([sQuery(id+"F0.wireOp",EDGE,"E1"),subQ0,sQuery(id+"F10.wireOp",EDGE,"E16.top"),sQuery(id+"F10.wireOp",EDGE,"E16.left"),sQuery(id+"F10.wireOp",EDGE,"E16.right"),sQuery(id+"F10.wireOp",EDGE,"E20"),sQuery(id+"F10.wireOp",EDGE,"E21"),sQuery(id+"F10.wireOp",EDGE,"E22"),sQuery(id+"F10.wireOp",EDGE,"E23"),sQuery(id+"F10.wireOp",EDGE,"E24"),sQuery(id+"F10.wireOp",EDGE,"E25")])],"isStart":true})]})],"blendedInto":[makeQuery(id+"F11.boolean.opBoolean","MERGE",FACE,{"derivedFrom":[makeQuery(id+"F3.boolean.opBoolean","MERGE",FACE,{"derivedFrom":[makeQuery(id+"F1.opRevolve","SWEPT_FACE",FACE,{"disambiguationData":[OSD([subQ0])]}),makeQuery(id+"F3.opExtrude","CAP_FACE",FACE,{"disambiguationData":[OSD([subQ4,subQ2,subQ1,subQ3])],"isStart":false}),makeQuery(id+"F3.opExtrude","CAP_FACE",FACE,{"disambiguationData":[OSD([sQuery(id+"F2.wireOp",EDGE,"E9.right"),subQ2,subQ1,sQuery(id+"F2.wireOp",EDGE,"E11.right")])],"isStart":false})]}),makeQuery(id+"F11.opExtrude","CAP_FACE",FACE,{"disambiguationData":[OSD([sQuery(id+"F0.wireOp",EDGE,"E1"),subQ0,sQuery(id+"F10.wireOp",EDGE,"E16.top"),sQuery(id+"F10.wireOp",EDGE,"E16.left"),sQuery(id+"F10.wireOp",EDGE,"E16.right"),sQuery(id+"F10.wireOp",EDGE,"E20"),sQuery(id+"F10.wireOp",EDGE,"E21"),sQuery(id+"F10.wireOp",EDGE,"E22"),sQuery(id+"F10.wireOp",EDGE,"E23"),sQuery(id+"F10.wireOp",EDGE,"E24"),sQuery(id+"F10.wireOp",EDGE,"E25")])],"isStart":true})]})]}),"instanceName":"1"});}
            var Q4;
            {var subQ0=sQuery(id+"F0.wireOp",EDGE,"E2");var subQ1=sQuery(id+"F2.wireOp",EDGE,"E11.right");var subQ2=sQuery(id+"F2.wireOp",EDGE,"E11.top");var subQ3=sQuery(id+"F2.wireOp",EDGE,"E11.bottom");var subQ4=sQuery(id+"F2.wireOp",EDGE,"E9.right");Q4=makeQuery(id+"F19.opPattern","COPY",EDGE,{"derivedFrom":makeQuery(id+"F17.opChamfer","BLEND_EDGE",EDGE,{"blendedFrom":[makeQuery(id+"F3.opExtrude","CAP_EDGE",EDGE,{"disambiguationData":[OSD([subQ3]),TDD([makeQuery(id+"F2.imprint","IMPRINT",EDGE,{"disambiguationData":[TD([[makeQuery(id+"F2.imprint","INTERSECT",VERTEX,{"derivedFrom":[subQ4,subQ3]}),-1.0]])],"derivedFrom":subQ3})])],"isStart":false}),makeQuery(id+"F11.boolean.opBoolean","MERGE",FACE,{"derivedFrom":[makeQuery(id+"F3.boolean.opBoolean","MERGE",FACE,{"derivedFrom":[makeQuery(id+"F1.opRevolve","SWEPT_FACE",FACE,{"disambiguationData":[OSD([subQ0])]}),makeQuery(id+"F3.opExtrude","CAP_FACE",FACE,{"disambiguationData":[OSD([sQuery(id+"F2.wireOp",EDGE,"E9.left"),subQ3,subQ2,sQuery(id+"F2.wireOp",EDGE,"E11.left")])],"isStart":false}),makeQuery(id+"F3.opExtrude","CAP_FACE",FACE,{"disambiguationData":[OSD([subQ4,subQ3,subQ2,subQ1])],"isStart":false})]}),makeQuery(id+"F11.opExtrude","CAP_FACE",FACE,{"disambiguationData":[OSD([sQuery(id+"F0.wireOp",EDGE,"E1"),subQ0,sQuery(id+"F10.wireOp",EDGE,"E16.top"),sQuery(id+"F10.wireOp",EDGE,"E16.left"),sQuery(id+"F10.wireOp",EDGE,"E16.right"),sQuery(id+"F10.wireOp",EDGE,"E20"),sQuery(id+"F10.wireOp",EDGE,"E21"),sQuery(id+"F10.wireOp",EDGE,"E22"),sQuery(id+"F10.wireOp",EDGE,"E23"),sQuery(id+"F10.wireOp",EDGE,"E24"),sQuery(id+"F10.wireOp",EDGE,"E25")])],"isStart":true})]})],"blendedInto":[makeQuery(id+"F11.boolean.opBoolean","MERGE",FACE,{"derivedFrom":[makeQuery(id+"F3.boolean.opBoolean","MERGE",FACE,{"derivedFrom":[makeQuery(id+"F1.opRevolve","SWEPT_FACE",FACE,{"disambiguationData":[OSD([subQ0])]}),makeQuery(id+"F3.opExtrude","CAP_FACE",FACE,{"disambiguationData":[OSD([sQuery(id+"F2.wireOp",EDGE,"E9.left"),subQ3,subQ2,sQuery(id+"F2.wireOp",EDGE,"E11.left")])],"isStart":false}),makeQuery(id+"F3.opExtrude","CAP_FACE",FACE,{"disambiguationData":[OSD([subQ4,subQ3,subQ2,subQ1])],"isStart":false})]}),makeQuery(id+"F11.opExtrude","CAP_FACE",FACE,{"disambiguationData":[OSD([sQuery(id+"F0.wireOp",EDGE,"E1"),subQ0,sQuery(id+"F10.wireOp",EDGE,"E16.top"),sQuery(id+"F10.wireOp",EDGE,"E16.left"),sQuery(id+"F10.wireOp",EDGE,"E16.right"),sQuery(id+"F10.wireOp",EDGE,"E20"),sQuery(id+"F10.wireOp",EDGE,"E21"),sQuery(id+"F10.wireOp",EDGE,"E22"),sQuery(id+"F10.wireOp",EDGE,"E23"),sQuery(id+"F10.wireOp",EDGE,"E24"),sQuery(id+"F10.wireOp",EDGE,"E25")])],"isStart":true})]})]}),"instanceName":"1"});}
            var Q5;
            Q5=makeQuery(id+"F19.opPattern","COPY",EDGE,{"derivedFrom":makeQuery(id+"F15.boolean.opBoolean","COPY",EDGE,{"derivedFrom":makeQuery(id+"F15.opExtrude","CAP_EDGE",EDGE,{"disambiguationData":[OSD([sQuery(id+"F13.wireOp",EDGE,"E29")])],"isStart":false})}),"instanceName":"1"});
            var Q6;
            Q6=makeQuery(id+"F19.opPattern","COPY",EDGE,{"derivedFrom":makeQuery(id+"F15.boolean.opBoolean","COPY",EDGE,{"derivedFrom":makeQuery(id+"F15.opExtrude","SWEPT_EDGE",EDGE,{"disambiguationData":[OSD([sQuery(id+"F10.wireOp",EDGE,"E20"),sQuery(id+"F13.wireOp",EDGE,"E29"),sQuery(id+"F13.wireOp",EDGE,"E30")])]})}),"instanceName":"1"});
            var Q7;
            Q7=makeQuery(id+"F19.opPattern","COPY",EDGE,{"derivedFrom":makeQuery(id+"F15.boolean.opBoolean","COPY",EDGE,{"derivedFrom":makeQuery(id+"F15.opExtrude","CAP_EDGE",EDGE,{"disambiguationData":[OSD([sQuery(id+"F13.wireOp",EDGE,"E29")])],"isStart":true})}),"instanceName":"1"});
            var Q8;
            Q8=makeQuery(id+"F19.opPattern","COPY",EDGE,{"derivedFrom":makeQuery(id+"F15.boolean.opBoolean","COPY",EDGE,{"derivedFrom":makeQuery(id+"F15.opExtrude","SWEPT_EDGE",EDGE,{"disambiguationData":[OSD([sQuery(id+"F10.wireOp",EDGE,"E20"),sQuery(id+"F13.wireOp",EDGE,"E28.5"),sQuery(id+"F13.wireOp",EDGE,"E29")])]})}),"instanceName":"1"});
            var Q9;
            Q9=makeQuery(id+"F19.opPattern","COPY",EDGE,{"derivedFrom":makeQuery(id+"F11.opExtrude","CAP_EDGE",EDGE,{"disambiguationData":[OSD([sQuery(id+"F10.wireOp",EDGE,"E24")])],"isStart":true}),"instanceName":"1"});
            var Q10;
            Q10=makeQuery(id+"F19.opPattern","COPY",EDGE,{"derivedFrom":makeQuery(id+"F11.opExtrude","CAP_EDGE",EDGE,{"disambiguationData":[OSD([sQuery(id+"F10.wireOp",EDGE,"E22")])],"isStart":false}),"instanceName":"1"});
            var Q11;
            Q11=makeQuery(id+"F22.opFillet","BLEND_EDGE",EDGE,{"blendedFrom":[makeQuery(id+"F19.opPattern","COPY",EDGE,{"derivedFrom":makeQuery(id+"F12.boolean.opBoolean","INTERSECT",EDGE,{"derivedFrom":[makeQuery(id+"F11.opExtrude","CAP_FACE",FACE,{"disambiguationData":[OSD([sQuery(id+"F0.wireOp",EDGE,"E1"),sQuery(id+"F0.wireOp",EDGE,"E2"),sQuery(id+"F10.wireOp",EDGE,"E16.top"),sQuery(id+"F10.wireOp",EDGE,"E16.left"),sQuery(id+"F10.wireOp",EDGE,"E16.right"),sQuery(id+"F10.wireOp",EDGE,"E20"),sQuery(id+"F10.wireOp",EDGE,"E21"),sQuery(id+"F10.wireOp",EDGE,"E22"),sQuery(id+"F10.wireOp",EDGE,"E23"),sQuery(id+"F10.wireOp",EDGE,"E24"),sQuery(id+"F10.wireOp",EDGE,"E25")])],"isStart":false}),makeQuery(id+"F12.opExtrude","SWEPT_FACE",FACE,{"disambiguationData":[OSD([sQuery(id+"F10.wireOp",EDGE,"E17")])]})]}),"instanceName":"1"}),makeQuery(id+"F19.opPattern","COPY",FACE,{"derivedFrom":makeQuery(id+"F12.opExtrude","SWEPT_FACE",FACE,{"disambiguationData":[OSD([sQuery(id+"F10.wireOp",EDGE,"E19")])]}),"instanceName":"1"})],"blendedInto":[makeQuery(id+"F19.opPattern","COPY",FACE,{"derivedFrom":makeQuery(id+"F12.opExtrude","SWEPT_FACE",FACE,{"disambiguationData":[OSD([sQuery(id+"F10.wireOp",EDGE,"E19")])]}),"instanceName":"1"})]});
            var Q12;
            Q12=makeQuery(id+"F22.opFillet","BLEND_EDGE",EDGE,{"blendedFrom":[makeQuery(id+"F19.opPattern","COPY",EDGE,{"derivedFrom":makeQuery(id+"F12.boolean.opBoolean","INTERSECT",EDGE,{"derivedFrom":[makeQuery(id+"F11.opExtrude","CAP_FACE",FACE,{"disambiguationData":[OSD([sQuery(id+"F0.wireOp",EDGE,"E1"),sQuery(id+"F0.wireOp",EDGE,"E2"),sQuery(id+"F10.wireOp",EDGE,"E16.top"),sQuery(id+"F10.wireOp",EDGE,"E16.left"),sQuery(id+"F10.wireOp",EDGE,"E16.right"),sQuery(id+"F10.wireOp",EDGE,"E20"),sQuery(id+"F10.wireOp",EDGE,"E21"),sQuery(id+"F10.wireOp",EDGE,"E22"),sQuery(id+"F10.wireOp",EDGE,"E23"),sQuery(id+"F10.wireOp",EDGE,"E24"),sQuery(id+"F10.wireOp",EDGE,"E25")])],"isStart":false}),makeQuery(id+"F12.opExtrude","SWEPT_FACE",FACE,{"disambiguationData":[OSD([sQuery(id+"F10.wireOp",EDGE,"E17")])]})]}),"instanceName":"1"}),makeQuery(id+"F19.opPattern","COPY",FACE,{"derivedFrom":makeQuery(id+"F12.opExtrude","SWEPT_FACE",FACE,{"disambiguationData":[OSD([sQuery(id+"F10.wireOp",EDGE,"E18")])]}),"instanceName":"1"})],"blendedInto":[makeQuery(id+"F19.opPattern","COPY",FACE,{"derivedFrom":makeQuery(id+"F12.opExtrude","SWEPT_FACE",FACE,{"disambiguationData":[OSD([sQuery(id+"F10.wireOp",EDGE,"E18")])]}),"instanceName":"1"})]});
            fillet(context, id + "F23", {"entities" : qUnion([Q0, Q1, Q2, Q3, Q4, Q5, Q6, Q7, Q8, Q9, Q10, Q11, Q12]), "radius" : 1 * mm, "tangentPropagation" : true, "allowEdgeOverflow" : false});
        }
        {
            var Q0;
            Q0=makeQuery(id+"F19.opPattern","COPY",BODY,{"derivedFrom":makeQuery(id+"F1.opRevolve","SWEPT_BODY",BODY,{"disambiguationData":[OSD([sQuery(id+"F0.wireOp",EDGE,"E0"),sQuery(id+"F0.wireOp",EDGE,"E1"),sQuery(id+"F0.wireOp",EDGE,"E2"),sQuery(id+"F0.wireOp",EDGE,"E3"),sQuery(id+"F0.wireOp",EDGE,"E4"),sQuery(id+"F0.wireOp",EDGE,"E6"),sQuery(id+"F0.wireOp",EDGE,"E7"),sQuery(id+"F0.wireOp",EDGE,"E8")])]}),"instanceName":"1"});
            transform(context, id + "F24", {"entities" : qUnion([Q0]), "transformType" : TransformType.TRANSLATION_3D, "dx" : 0 * mm, "dy" : 0 * mm, "dz" : 0 * mm, "makeCopy" : true});
        }
        {
            var Q0;
            Q0=makeQuery(id+"F19.opPattern","COPY",BODY,{"derivedFrom":makeQuery(id+"F1.opRevolve","SWEPT_BODY",BODY,{"disambiguationData":[OSD([sQuery(id+"F0.wireOp",EDGE,"E0"),sQuery(id+"F0.wireOp",EDGE,"E1"),sQuery(id+"F0.wireOp",EDGE,"E2"),sQuery(id+"F0.wireOp",EDGE,"E3"),sQuery(id+"F0.wireOp",EDGE,"E4"),sQuery(id+"F0.wireOp",EDGE,"E6"),sQuery(id+"F0.wireOp",EDGE,"E7"),sQuery(id+"F0.wireOp",EDGE,"E8")])]}),"instanceName":"1"});
            deleteBodies(context, id + "F25", {"entities" : qUnion([Q0])});
        }
    });
